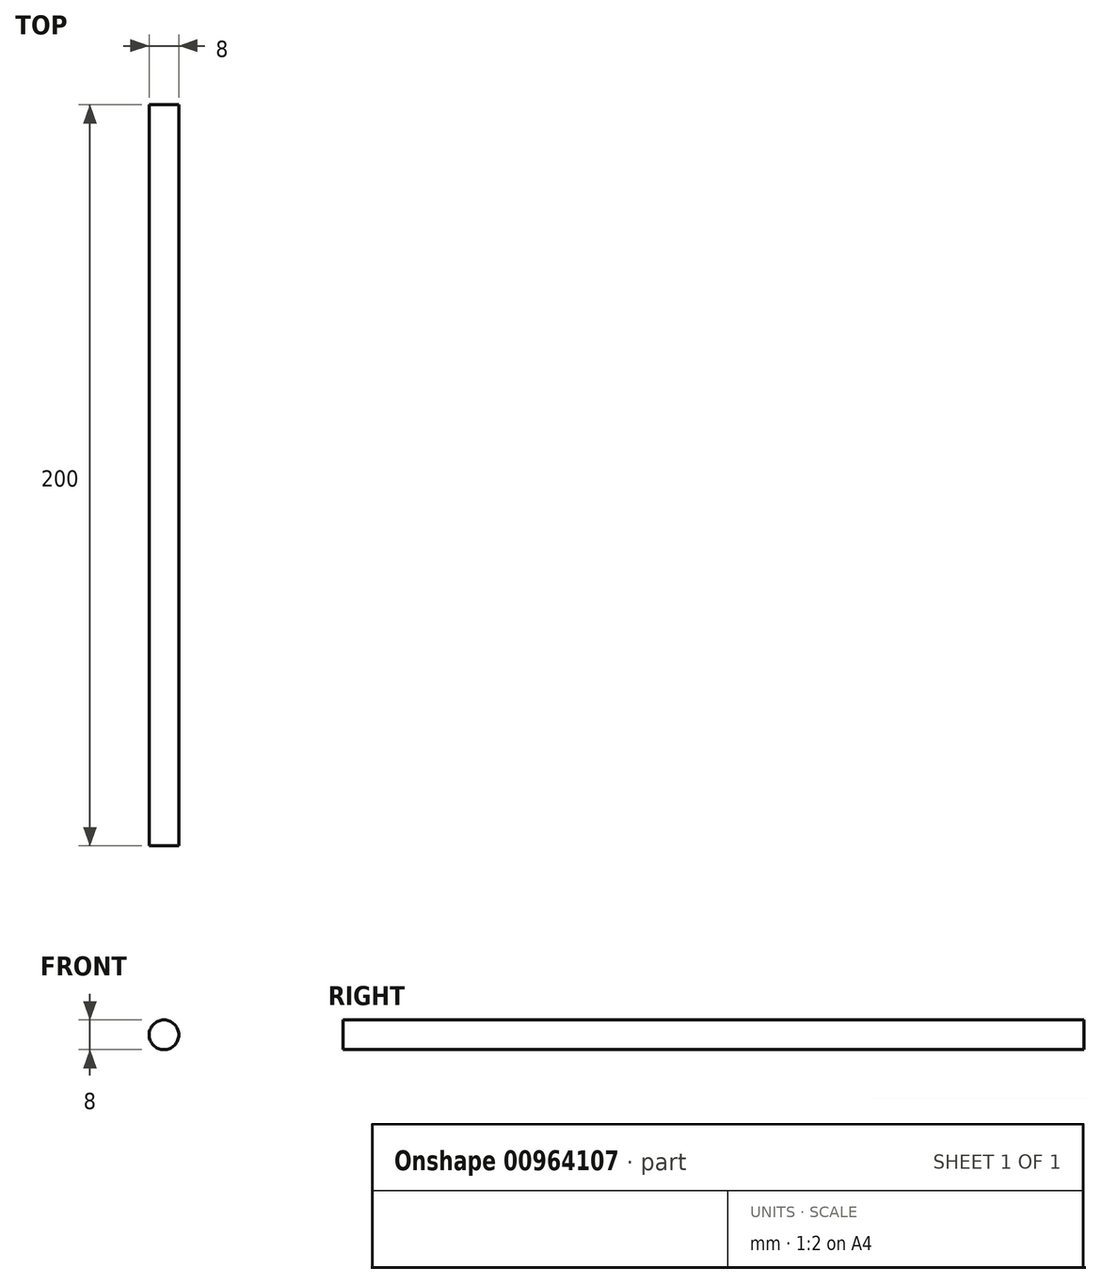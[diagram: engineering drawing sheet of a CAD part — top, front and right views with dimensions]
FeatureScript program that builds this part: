
annotation { "Feature Type Name" : "Feature", "Feature Type Description" : "" }
export const myFeature = defineFeature(function(context is Context, id is Id, definition is map)
    precondition{}
    {
        {
            var Q0;
            Q0=qCreatedBy(makeId("Front.planeOp"),FACE);
            var sketch = newSketch(context, id + "F0", { "sketchPlane" : qUnion([Q0])});
            skCircle(sketch, "E0", {"center": v(0, 0) * mm, "radius": 4 * mm});
            skSolve(sketch);
        }
        {
            var Q0;
            Q0 = qSketchRegion(id + "F0", true);
            extrude(context, id + "F1", {"entities" : qUnion([Q0]), "depth" : 200 * mm, "offsetDistance" : 25 * mm});
        }
    });
